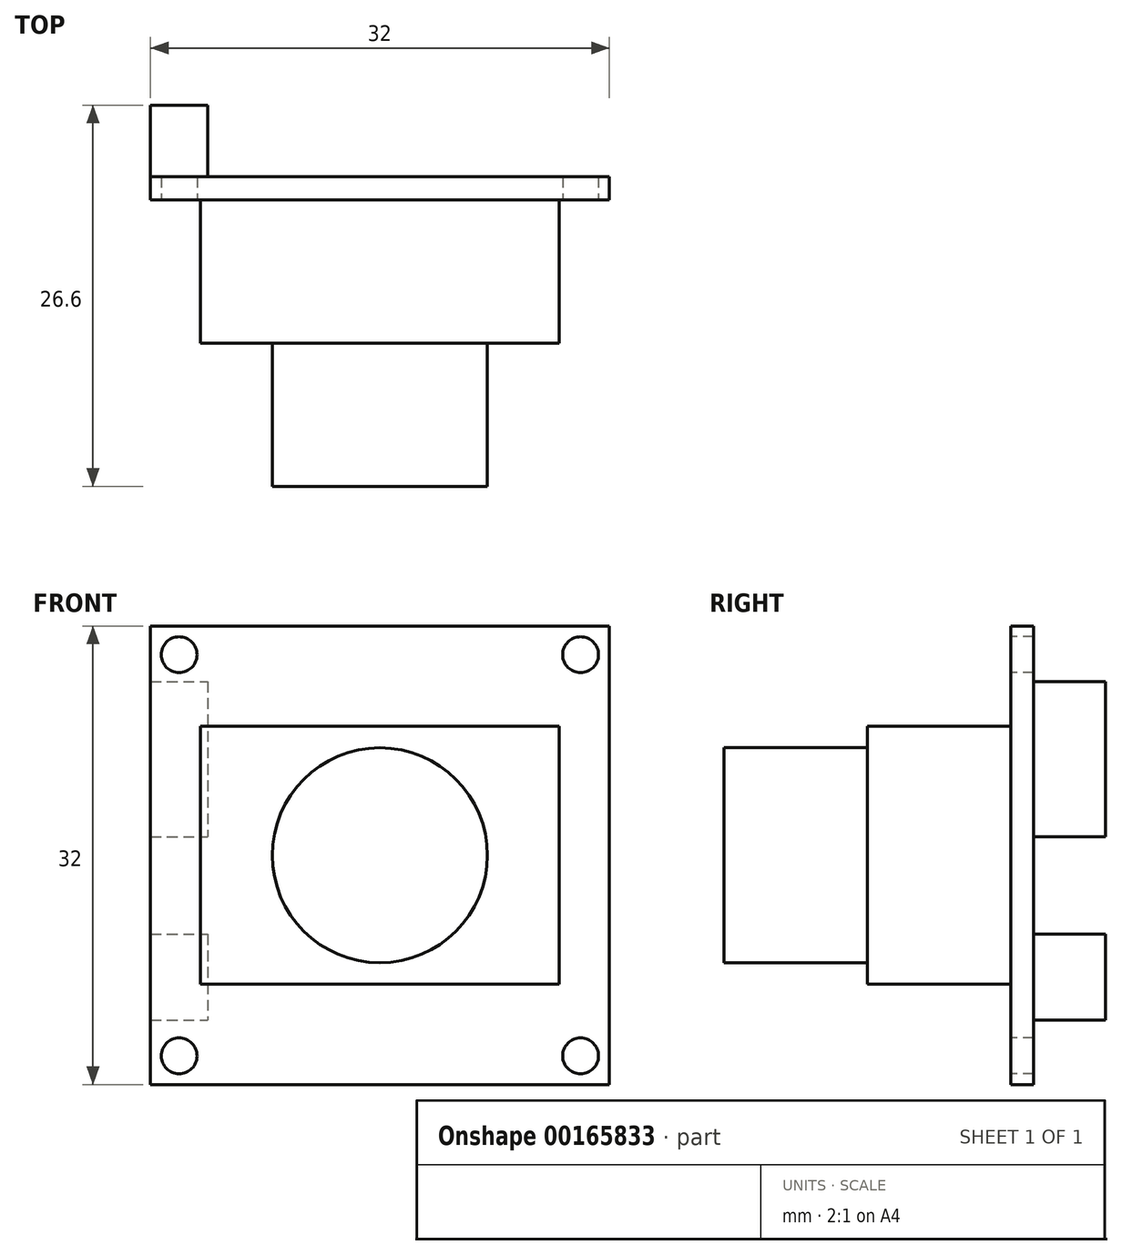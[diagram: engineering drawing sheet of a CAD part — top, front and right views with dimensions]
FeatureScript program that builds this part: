
annotation { "Feature Type Name" : "Feature", "Feature Type Description" : "" }
export const myFeature = defineFeature(function(context is Context, id is Id, definition is map)
    precondition{}
    {
        {
            var Q0;
            Q0=qCreatedBy(makeId("Front.planeOp"),FACE);
            var sketch = newSketch(context, id + "F0", { "sketchPlane" : qUnion([Q0])});
            skLineSegment(sketch, "E0.bottom", {"start": v(16, 16) * mm, "end": v(-16, 16) * mm});
            skLineSegment(sketch, "E0.top", {"start": v(16, -16) * mm, "end": v(-16, -16) * mm});
            skLineSegment(sketch, "E0.left", {"start": v(16, 16) * mm, "end": v(16, -16) * mm});
            skLineSegment(sketch, "E0.right", {"start": v(-16, 16) * mm, "end": v(-16, -16) * mm});
            skPoint(sketch, "E0.middle", {"position": v(0, 0) * mm});
            skSolve(sketch);
        }
        {
            var Q0;
            Q0 = qSketchRegion(id + "F0", true);
            extrude(context, id + "F1", {"entities" : qUnion([Q0]), "depth" : 1.6 * mm});
        }
        {
            var Q0;
            Q0=makeQuery(id+"F1.opExtrude","CAP_FACE",FACE,{"disambiguationData":[OSD([sQuery(id+"F0.wireOp",EDGE,"E0.bottom"),sQuery(id+"F0.wireOp",EDGE,"E0.top"),sQuery(id+"F0.wireOp",EDGE,"E0.left"),sQuery(id+"F0.wireOp",EDGE,"E0.right")])],"isStart":false});
            var sketch = newSketch(context, id + "F2", { "sketchPlane" : qUnion([Q0])});
            skLineSegment(sketch, "E1.bottom", {"start": v(12.5, 9) * mm, "end": v(-12.5, 9) * mm});
            skLineSegment(sketch, "E1.top", {"start": v(12.5, -9) * mm, "end": v(-12.5, -9) * mm});
            skLineSegment(sketch, "E1.left", {"start": v(12.5, 9) * mm, "end": v(12.5, -9) * mm});
            skLineSegment(sketch, "E1.right", {"start": v(-12.5, 9) * mm, "end": v(-12.5, -9) * mm});
            skPoint(sketch, "E1.middle", {"position": v(0, 0) * mm});
            skSolve(sketch);
        }
        {
            var Q0;
            Q0 = qSketchRegion(id + "F2", true);
            extrude(context, id + "F3", {"entities" : qUnion([Q0]), "operationType" : NewBodyOperationType.ADD, "depth" : 10 * mm});
        }
        {
            var Q0;
            Q0=makeQuery(id+"F3.opExtrude","CAP_FACE",FACE,{"disambiguationData":[OSD([sQuery(id+"F2.wireOp",EDGE,"E1.bottom"),sQuery(id+"F2.wireOp",EDGE,"E1.top"),sQuery(id+"F2.wireOp",EDGE,"E1.left"),sQuery(id+"F2.wireOp",EDGE,"E1.right")])],"isStart":false});
            var sketch = newSketch(context, id + "F4", { "sketchPlane" : qUnion([Q0])});
            skCircle(sketch, "E2", {"center": v(0, 0) * mm, "radius": 7.5 * mm});
            skSolve(sketch);
        }
        {
            var Q0;
            Q0 = qSketchRegion(id + "F4", true);
            extrude(context, id + "F5", {"entities" : qUnion([Q0]), "operationType" : NewBodyOperationType.ADD, "depth" : 10 * mm});
        }
        {
            var Q0;
            Q0=makeQuery(id+"F1.opExtrude","CAP_FACE",FACE,{"disambiguationData":[OSD([sQuery(id+"F0.wireOp",EDGE,"E0.bottom"),sQuery(id+"F0.wireOp",EDGE,"E0.top"),sQuery(id+"F0.wireOp",EDGE,"E0.left"),sQuery(id+"F0.wireOp",EDGE,"E0.right")])],"isStart":true});
            var sketch = newSketch(context, id + "F6", { "sketchPlane" : qUnion([Q0])});
            skLineSegment(sketch, "E3.bottom", {"start": v(16, 12.12) * mm, "end": v(12, 12.12) * mm});
            skLineSegment(sketch, "E3.top", {"start": v(16, 1.28) * mm, "end": v(12, 1.28) * mm});
            skLineSegment(sketch, "E3.left", {"start": v(16, 12.12) * mm, "end": v(16, 1.28) * mm});
            skLineSegment(sketch, "E3.right", {"start": v(12, 12.12) * mm, "end": v(12, 1.28) * mm});
            skLineSegment(sketch, "E4.bottom", {"start": v(16, -5.5) * mm, "end": v(12, -5.5) * mm});
            skLineSegment(sketch, "E4.top", {"start": v(16, -11.5) * mm, "end": v(12, -11.5) * mm});
            skLineSegment(sketch, "E4.left", {"start": v(16, -5.5) * mm, "end": v(16, -11.5) * mm});
            skLineSegment(sketch, "E4.right", {"start": v(12, -5.5) * mm, "end": v(12, -11.5) * mm});
            skSolve(sketch);
        }
        {
            var Q0;
            Q0 = qSketchRegion(id + "F6", true);
            extrude(context, id + "F7", {"entities" : qUnion([Q0]), "operationType" : NewBodyOperationType.ADD, "depth" : 5 * mm});
        }
        {
            var Q0;
            Q0=makeQuery(id+"F1.opExtrude","CAP_FACE",FACE,{"disambiguationData":[OSD([sQuery(id+"F0.wireOp",EDGE,"E0.bottom"),sQuery(id+"F0.wireOp",EDGE,"E0.top"),sQuery(id+"F0.wireOp",EDGE,"E0.left"),sQuery(id+"F0.wireOp",EDGE,"E0.right")])],"isStart":false});
            var sketch = newSketch(context, id + "F8", { "sketchPlane" : qUnion([Q0])});
            skCircle(sketch, "E5", {"center": v(14, 14) * mm, "radius": 1.25 * mm});
            skCircle(sketch, "E6", {"center": v(14, -14) * mm, "radius": 1.25 * mm});
            skCircle(sketch, "E7", {"center": v(-14, -14) * mm, "radius": 1.25 * mm});
            skCircle(sketch, "E8", {"center": v(-14, 14) * mm, "radius": 1.25 * mm});
            skSolve(sketch);
        }
        {
            var Q0;
            Q0 = qSketchRegion(id + "F8", true);
            extrude(context, id + "F9", {"entities" : qUnion([Q0]), "operationType" : NewBodyOperationType.REMOVE, "oppositeDirection" : true, "depth" : 25 * mm});
        }
    });
